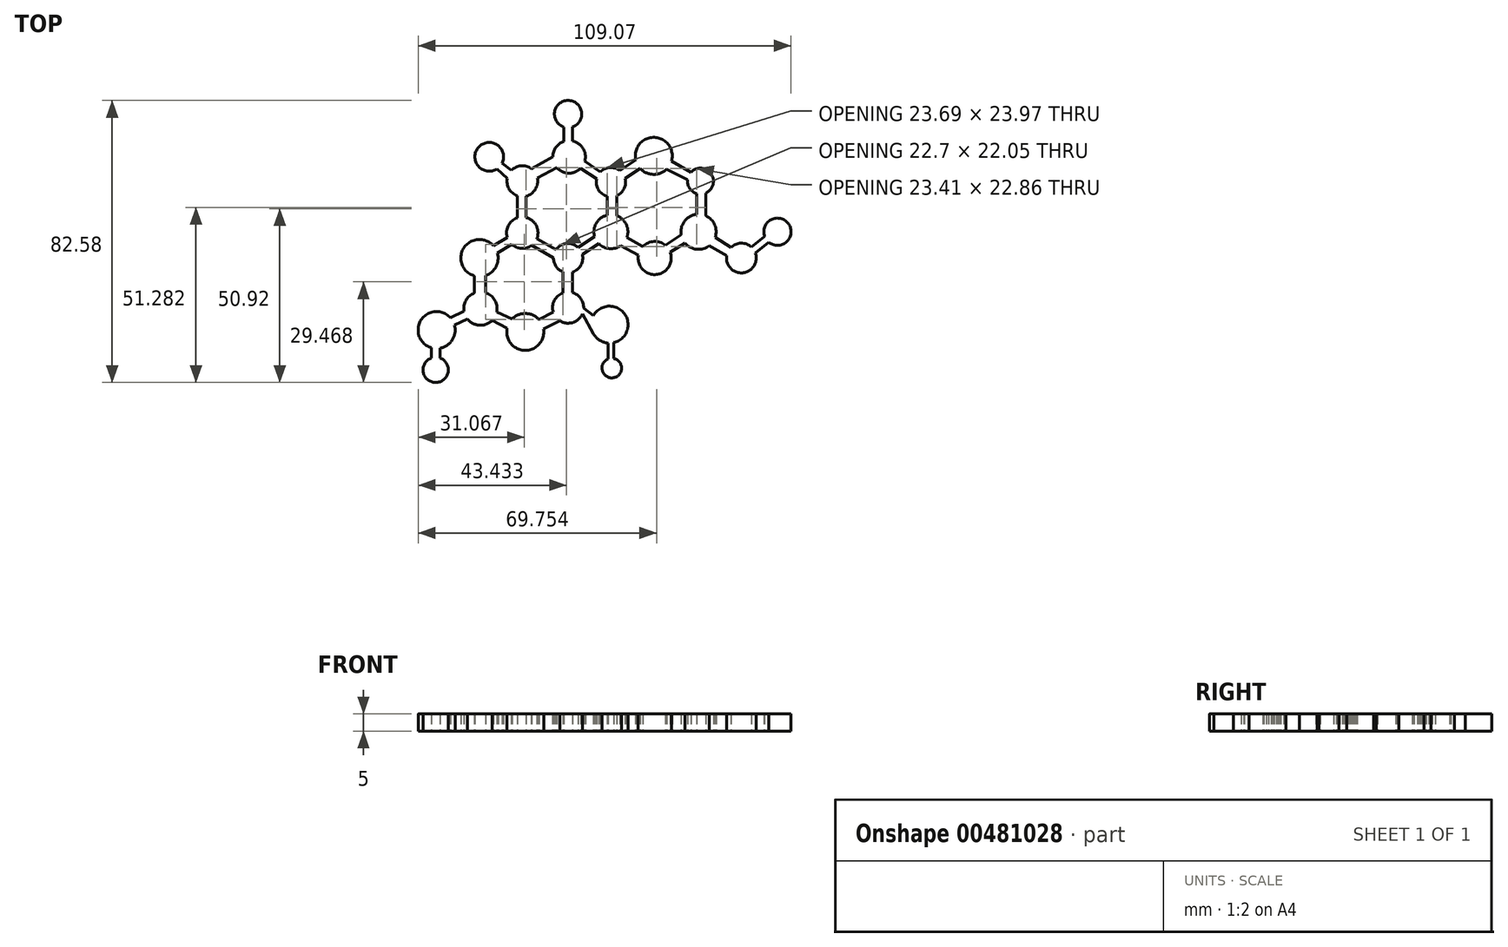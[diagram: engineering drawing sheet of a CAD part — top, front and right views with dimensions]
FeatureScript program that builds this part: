
annotation { "Feature Type Name" : "Feature", "Feature Type Description" : "" }
export const myFeature = defineFeature(function(context is Context, id is Id, definition is map)
    precondition{}
    {
        {
            var Q0;
            Q0=qCreatedBy(makeId("Top.planeOp"),FACE);
            var sketch = newSketch(context, id + "F0", { "sketchPlane" : qUnion([Q0])});
            skCircle(sketch, "E0", {"center": v(-7.12, 29.61) * mm, "radius": 4.77 * mm});
            skCircle(sketch, "E1", {"center": v(-20.78, 22.5) * mm, "radius": 4.5 * mm});
            skCircle(sketch, "E2", {"center": v(-20.79, 7.4) * mm, "radius": 4.6 * mm});
            skCircle(sketch, "E3", {"center": v(-7.4, 0) * mm, "radius": 4.28 * mm});
            skCircle(sketch, "E4", {"center": v(-7.4, -14.52) * mm, "radius": 4.56 * mm});
            skCircle(sketch, "E5", {"center": v(4.73, -19.5) * mm, "radius": 5.42 * mm});
            skCircle(sketch, "E6", {"center": v(5.39, -32.22) * mm, "radius": 2.86 * mm});
            skCircle(sketch, "E7", {"center": v(-45.84, -21.07) * mm, "radius": 5.42 * mm});
            skCircle(sketch, "E8", {"center": v(-46.13, -32.74) * mm, "radius": 3.7 * mm});
            skCircle(sketch, "E9", {"center": v(-33.03, -14.8) * mm, "radius": 4.87 * mm});
            skCircle(sketch, "E10", {"center": v(-19.93, -21.64) * mm, "radius": 5.4 * mm});
            skCircle(sketch, "E11", {"center": v(-33.31, 0) * mm, "radius": 5.44 * mm});
            skCircle(sketch, "E12", {"center": v(5.13, 22.21) * mm, "radius": 4.27 * mm});
            skCircle(sketch, "E13", {"center": v(17.66, 29.9) * mm, "radius": 5.4 * mm});
            skCircle(sketch, "E14", {"center": v(31.33, 22.5) * mm, "radius": 3.8 * mm});
            skCircle(sketch, "E15", {"center": v(30.76, 7.69) * mm, "radius": 5.14 * mm});
            skCircle(sketch, "E16", {"center": v(17.94, 0) * mm, "radius": 4.85 * mm});
            skCircle(sketch, "E17", {"center": v(5.13, 7.69) * mm, "radius": 4.97 * mm});
            skCircle(sketch, "E18", {"center": v(43.28, 0) * mm, "radius": 4.35 * mm});
            skCircle(sketch, "E19", {"center": v(53.82, 7.69) * mm, "radius": 3.99 * mm});
            skCircle(sketch, "E20", {"center": v(-7.4, 42.14) * mm, "radius": 3.99 * mm});
            skCircle(sketch, "E21", {"center": v(-30.46, 29.62) * mm, "radius": 4.2 * mm});
            skLineSegment(sketch, "E22", {"start": v(-28.25, 26.04) * mm, "end": v(-25.2, 23.34) * mm});
            skLineSegment(sketch, "E23", {"start": v(-24, 25.65) * mm, "end": v(-26.67, 27.8) * mm});
            skLineSegment(sketch, "E24", {"start": v(-18.13, 26.13) * mm, "end": v(-11.89, 29.7) * mm});
            skLineSegment(sketch, "E25", {"start": v(-16.37, 23.4) * mm, "end": v(-10.7, 26.45) * mm});
            skLineSegment(sketch, "E26", {"start": v(-8.61, 34.15) * mm, "end": v(-8.61, 38.34) * mm});
            skLineSegment(sketch, "E27", {"start": v(-6.12, 38.37) * mm, "end": v(-6.12, 34.28) * mm});
            skLineSegment(sketch, "E28", {"start": v(-2.51, 28.35) * mm, "end": v(2.03, 25.15) * mm});
            skLineSegment(sketch, "E29", {"start": v(0.96, 23.12) * mm, "end": v(-3.7, 26.27) * mm});
            skLineSegment(sketch, "E30", {"start": v(7.77, 25.57) * mm, "end": v(12.38, 28.72) * mm});
            skLineSegment(sketch, "E31", {"start": v(13.65, 26.26) * mm, "end": v(9.25, 23.35) * mm});
            skLineSegment(sketch, "E32", {"start": v(21.39, 25.98) * mm, "end": v(27.55, 22.88) * mm});
            skLineSegment(sketch, "E33", {"start": v(28.58, 25.12) * mm, "end": v(22.84, 28.33) * mm});
            skLineSegment(sketch, "E34", {"start": v(30.2, 18.87) * mm, "end": v(30.2, 12.8) * mm});
            skLineSegment(sketch, "E35", {"start": v(32.88, 19.03) * mm, "end": v(32.88, 12.37) * mm});
            skLineSegment(sketch, "E36", {"start": v(26.82, 4.39) * mm, "end": v(22.49, 1.67) * mm});
            skLineSegment(sketch, "E37", {"start": v(21.05, 3.72) * mm, "end": v(25.7, 6.81) * mm});
            skLineSegment(sketch, "E38", {"start": v(9.8, 6) * mm, "end": v(14.49, 3.4) * mm});
            skLineSegment(sketch, "E39", {"start": v(13.16, 0.8) * mm, "end": v(8.02, 3.64) * mm});
            skLineSegment(sketch, "E40", {"start": v(6.79, 12.38) * mm, "end": v(6.79, 18.28) * mm});
            skLineSegment(sketch, "E41", {"start": v(4.02, 18.09) * mm, "end": v(4.02, 12.54) * mm});
            skLineSegment(sketch, "E42", {"start": v(-4.43, 3.09) * mm, "end": v(0.35, 6.34) * mm});
            skLineSegment(sketch, "E43", {"start": v(1.6, 4.19) * mm, "end": v(-3.25, 1.06) * mm});
            skLineSegment(sketch, "E44", {"start": v(-10.89, 2.49) * mm, "end": v(-16.56, 5.6) * mm});
            skLineSegment(sketch, "E45", {"start": v(-18.08, 3.7) * mm, "end": v(-11.68, 0) * mm});
            skLineSegment(sketch, "E46", {"start": v(-19.67, 11.86) * mm, "end": v(-19.67, 18.13) * mm});
            skLineSegment(sketch, "E47", {"start": v(-22.28, 18.25) * mm, "end": v(-22.28, 11.75) * mm});
            skLineSegment(sketch, "E48", {"start": v(-29.27, 3.63) * mm, "end": v(-25.18, 6.09) * mm});
            skLineSegment(sketch, "E49", {"start": v(-23.91, 4.04) * mm, "end": v(-28.06, 1.4) * mm});
            skLineSegment(sketch, "E50", {"start": v(35.63, 6.05) * mm, "end": v(40.25, 3.11) * mm});
            skLineSegment(sketch, "E51", {"start": v(39, 0.75) * mm, "end": v(33.96, 3.67) * mm});
            skLineSegment(sketch, "E52", {"start": v(46.2, 3.21) * mm, "end": v(50.07, 6.33) * mm});
            skLineSegment(sketch, "E53", {"start": v(51.23, 4.66) * mm, "end": v(47.38, 1.44) * mm});
            skLineSegment(sketch, "E54", {"start": v(-34.83, -5.22) * mm, "end": v(-34.83, -10.28) * mm});
            skLineSegment(sketch, "E55", {"start": v(-31.54, -10.16) * mm, "end": v(-31.54, -5.14) * mm});
            skLineSegment(sketch, "E56", {"start": v(-28.25, -15.77) * mm, "end": v(-23.78, -17.83) * mm});
            skLineSegment(sketch, "E57", {"start": v(-25.23, -20.55) * mm, "end": v(-29.6, -18.27) * mm});
            skLineSegment(sketch, "E58", {"start": v(-15.92, -18) * mm, "end": v(-11.76, -15.84) * mm});
            skLineSegment(sketch, "E59", {"start": v(-9.78, -18.4) * mm, "end": v(-14.59, -20.8) * mm});
            skLineSegment(sketch, "E60", {"start": v(-8.84, -10.2) * mm, "end": v(-8.84, -4.03) * mm});
            skLineSegment(sketch, "E61", {"start": v(-6.14, -4.1) * mm, "end": v(-6.14, -10.14) * mm});
            skLineSegment(sketch, "E62", {"start": v(-40.6, -19.68) * mm, "end": v(-36.88, -17.8) * mm});
            skLineSegment(sketch, "E63", {"start": v(-37.85, -15.52) * mm, "end": v(-41.76, -17.5) * mm});
            skLineSegment(sketch, "E64", {"start": v(-44.86, -26.4) * mm, "end": v(-44.86, -29.27) * mm});
            skLineSegment(sketch, "E65", {"start": v(-47.33, -29.24) * mm, "end": v(-47.33, -26.28) * mm});
            skLineSegment(sketch, "E66", {"start": v(-3.23, -16.36) * mm, "end": v(0, -22.15) * mm});
            skLineSegment(sketch, "E67", {"start": v(0, -16.87) * mm, "end": v(-2.85, -14.65) * mm});
            skLineSegment(sketch, "E68", {"start": v(4.32, -29.57) * mm, "end": v(4.32, -24.9) * mm});
            skLineSegment(sketch, "E69", {"start": v(6.01, -24.77) * mm, "end": v(6.01, -29.43) * mm});
            skSolve(sketch);
        }
        {
            var Q0;
            Q0 = qSketchRegion(id + "F0", true);
            var Q1;
            {var subQ0=sQuery(id+"F0.wireOp",EDGE,"E44");Q1=makeQuery(id+"F0.imprint","IMPRINT",FACE,{"disambiguationData":[TD([[makeQuery(id+"F0.imprint","IMPRINT",EDGE,{"derivedFrom":subQ0}),1.0]])]});}
            var Q2;
            {var subQ0=sQuery(id+"F0.wireOp",EDGE,"E40");Q2=makeQuery(id+"F0.imprint","IMPRINT",FACE,{"disambiguationData":[TD([[makeQuery(id+"F0.imprint","IMPRINT",EDGE,{"derivedFrom":subQ0}),1.0]])]});}
            extrude(context, id + "F1", {"entities" : qUnion([Q0, Q1, Q2]), "depth" : 5 * mm});
        }
    });
